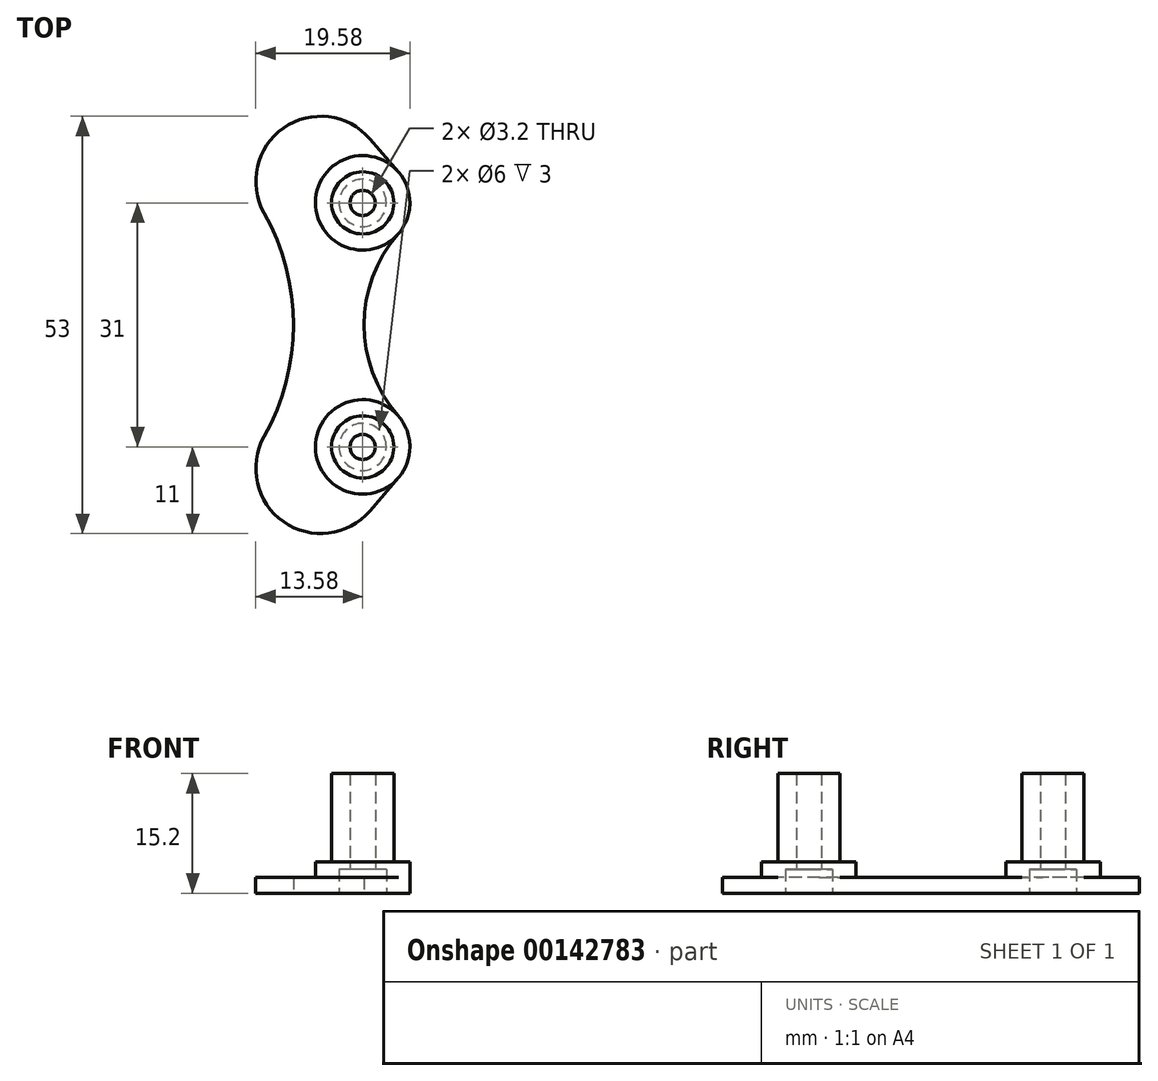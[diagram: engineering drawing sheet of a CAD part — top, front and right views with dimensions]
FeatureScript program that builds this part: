
annotation { "Feature Type Name" : "Feature", "Feature Type Description" : "" }
export const myFeature = defineFeature(function(context is Context, id is Id, definition is map)
    precondition{}
    {
        {
            var Q0;
            Q0=qCreatedBy(makeId("Top.planeOp"),FACE);
            var sketch = newSketch(context, id + "F0", { "sketchPlane" : qUnion([Q0])});
            skCircle(sketch, "E0", {"center": v(0, 15.5) * mm, "radius": 1.6 * mm});
            skCircle(sketch, "E1", {"center": v(0, 15.5) * mm, "radius": 3.95 * mm});
            skCircle(sketch, "E2", {"center": v(0, 15.5) * mm, "radius": 6 * mm});
            skCircle(sketch, "E3", {"center": v(0, -15.5) * mm, "radius": 1.6 * mm});
            skCircle(sketch, "E4", {"center": v(0, -15.5) * mm, "radius": 3.95 * mm});
            skCircle(sketch, "E5", {"center": v(0, -15.5) * mm, "radius": 6 * mm});
            skLineSegment(sketch, "E6", {"start": v(0, 15.5) * mm, "end": v(0, -15.5) * mm, "construction": true});
            skCircle(sketch, "E7", {"center": v(-5.33, 18.25) * mm, "radius": 8.25 * mm});
            skCircle(sketch, "E8", {"center": v(-5.33, -18.25) * mm, "radius": 8.25 * mm});
            skArc(sketch, "E9", {"start": v(-12.52, -14.2) * mm, "mid": v(-8.8, 0) * mm, "end": v(-12.52, 14.2) * mm});
            skArc(sketch, "E10", {"start": v(4.5, 11.54) * mm, "mid": v(0.16, 0) * mm, "end": v(4.5, -11.54) * mm});
            skLineSegment(sketch, "E11", {"start": v(-37.8, 0) * mm, "end": v(17.66, 0) * mm, "construction": true});
            skLineSegment(sketch, "E12", {"start": v(0.92, 23.63) * mm, "end": v(4.55, 19.41) * mm});
            skLineSegment(sketch, "E13", {"start": v(0.92, -23.63) * mm, "end": v(4.55, -19.41) * mm});
            skCircle(sketch, "E14", {"center": v(0, 15.5) * mm, "radius": 3 * mm});
            skCircle(sketch, "E15", {"center": v(0, -15.5) * mm, "radius": 3 * mm});
            skSolve(sketch);
        }
        {
            var Q0;
            {var subQ0=sQuery(id+"F0.wireOp",EDGE,"E9");Q0=makeQuery(id+"F0.imprint","IMPRINT",FACE,{"disambiguationData":[TD([[makeQuery(id+"F0.imprint","IMPRINT",EDGE,{"derivedFrom":subQ0}),-1.0]])]});}
            var Q1;
            {var subQ0=sQuery(id+"F0.wireOp",EDGE,"E8");var subQ1=sQuery(id+"F0.wireOp",EDGE,"E5");var subQ2=makeQuery(id+"F0.imprint","INTERSECT",VERTEX,{"disambiguationData":[OD(0.0)],"derivedFrom":[subQ1,subQ0]});Q1=makeQuery(id+"F0.imprint","IMPRINT",FACE,{"disambiguationData":[TD([[makeQuery(id+"F0.imprint","IMPRINT",EDGE,{"disambiguationData":[TD([[subQ2,-1.0]])],"derivedFrom":subQ1}),-1.0]])]});}
            var Q2;
            {var subQ2=sQuery(id+"F0.wireOp",EDGE,"E8");var subQ5=sQuery(id+"F0.wireOp",EDGE,"E4");var subQ6=makeQuery(id+"F0.imprint","INTERSECT",VERTEX,{"disambiguationData":[OD(0.0)],"derivedFrom":[subQ5,subQ2]});Q2=makeQuery(id+"F0.imprint","IMPRINT",FACE,{"disambiguationData":[TD([[makeQuery(id+"F0.imprint","IMPRINT",EDGE,{"disambiguationData":[TD([[subQ6,1.0]])],"derivedFrom":subQ5}),-1.0]])]});}
            var Q3;
            {var subQ3=sQuery(id+"F0.wireOp",EDGE,"E7");var subQ5=sQuery(id+"F0.wireOp",EDGE,"E1");var subQ8=makeQuery(id+"F0.imprint","INTERSECT",VERTEX,{"disambiguationData":[OD(0.0)],"derivedFrom":[subQ5,subQ3]});Q3=makeQuery(id+"F0.imprint","IMPRINT",FACE,{"disambiguationData":[TD([[makeQuery(id+"F0.imprint","IMPRINT",EDGE,{"disambiguationData":[TD([[subQ8,-1.0]])],"derivedFrom":subQ5}),-1.0]])]});}
            var Q4;
            {var subQ0=sQuery(id+"F0.wireOp",EDGE,"E8");var subQ1=sQuery(id+"F0.wireOp",EDGE,"E4");var subQ2=makeQuery(id+"F0.imprint","INTERSECT",VERTEX,{"disambiguationData":[OD(0.0)],"derivedFrom":[subQ1,subQ0]});Q4=makeQuery(id+"F0.imprint","IMPRINT",FACE,{"disambiguationData":[TD([[makeQuery(id+"F0.imprint","IMPRINT",EDGE,{"disambiguationData":[TD([[subQ2,-1.0]])],"derivedFrom":subQ1}),-1.0]])]});}
            var Q5;
            {var subQ0=sQuery(id+"F0.wireOp",EDGE,"E7");var subQ1=sQuery(id+"F0.wireOp",EDGE,"E2");var subQ2=makeQuery(id+"F0.imprint","INTERSECT",VERTEX,{"disambiguationData":[OD(0.0)],"derivedFrom":[subQ1,subQ0]});Q5=makeQuery(id+"F0.imprint","IMPRINT",FACE,{"disambiguationData":[TD([[makeQuery(id+"F0.imprint","IMPRINT",EDGE,{"disambiguationData":[TD([[subQ2,-1.0]])],"derivedFrom":subQ1}),-1.0]])]});}
            var Q6;
            {var subQ0=sQuery(id+"F0.wireOp",EDGE,"E7");var subQ1=sQuery(id+"F0.wireOp",EDGE,"E1");var subQ2=makeQuery(id+"F0.imprint","INTERSECT",VERTEX,{"disambiguationData":[OD(0.0)],"derivedFrom":[subQ1,subQ0]});Q6=makeQuery(id+"F0.imprint","IMPRINT",FACE,{"disambiguationData":[TD([[makeQuery(id+"F0.imprint","IMPRINT",EDGE,{"disambiguationData":[TD([[subQ2,1.0]])],"derivedFrom":subQ1}),-1.0]])]});}
            var Q7;
            Q7=makeQuery(id+"F0.imprint","IMPRINT",FACE,{"disambiguationData":[TD([[makeQuery(id+"F0.imprint","IMPRINT",EDGE,{"derivedFrom":sQuery(id+"F0.wireOp",EDGE,"E0")}),-1.0]])]});
            var Q8;
            Q8=makeQuery(id+"F0.imprint","IMPRINT",FACE,{"disambiguationData":[TD([[makeQuery(id+"F0.imprint","IMPRINT",EDGE,{"derivedFrom":sQuery(id+"F0.wireOp",EDGE,"E3")}),-1.0]])]});
            var Q9;
            Q9=makeQuery(id+"F0.imprint","IMPRINT",FACE,{"disambiguationData":[TD([[makeQuery(id+"F0.imprint","IMPRINT",EDGE,{"derivedFrom":sQuery(id+"F0.wireOp",EDGE,"E3")}),1.0]])]});
            var Q10;
            Q10=makeQuery(id+"F0.imprint","IMPRINT",FACE,{"disambiguationData":[TD([[makeQuery(id+"F0.imprint","IMPRINT",EDGE,{"derivedFrom":sQuery(id+"F0.wireOp",EDGE,"E0")}),1.0]])]});
            var Q11;
            {var subQ0=sQuery(id+"F0.wireOp",EDGE,"E8");var subQ1=sQuery(id+"F0.wireOp",EDGE,"E4");var subQ2=makeQuery(id+"F0.imprint","INTERSECT",VERTEX,{"disambiguationData":[OD(0.0)],"derivedFrom":[subQ1,subQ0]});Q11=makeQuery(id+"F0.imprint","IMPRINT",FACE,{"disambiguationData":[TD([[makeQuery(id+"F0.imprint","IMPRINT",EDGE,{"disambiguationData":[TD([[subQ2,1.0]])],"derivedFrom":subQ1}),1.0]])]});}
            var Q12;
            {var subQ0=sQuery(id+"F0.wireOp",EDGE,"E7");var subQ1=sQuery(id+"F0.wireOp",EDGE,"E1");var subQ2=makeQuery(id+"F0.imprint","INTERSECT",VERTEX,{"disambiguationData":[OD(0.0)],"derivedFrom":[subQ1,subQ0]});Q12=makeQuery(id+"F0.imprint","IMPRINT",FACE,{"disambiguationData":[TD([[makeQuery(id+"F0.imprint","IMPRINT",EDGE,{"disambiguationData":[TD([[subQ2,-1.0]])],"derivedFrom":subQ1}),1.0]])]});}
            var Q13;
            {var subQ0=sQuery(id+"F0.wireOp",EDGE,"E12");Q13=makeQuery(id+"F0.imprint","IMPRINT",FACE,{"disambiguationData":[TD([[makeQuery(id+"F0.imprint","IMPRINT",EDGE,{"derivedFrom":subQ0}),-1.0]])]});}
            var Q14;
            {var subQ0=sQuery(id+"F0.wireOp",EDGE,"E13");Q14=makeQuery(id+"F0.imprint","IMPRINT",FACE,{"disambiguationData":[TD([[makeQuery(id+"F0.imprint","IMPRINT",EDGE,{"derivedFrom":subQ0}),1.0]])]});}
            var Q15;
            {var subQ0=sQuery(id+"F0.wireOp",EDGE,"E7");var subQ1=sQuery(id+"F0.wireOp",EDGE,"E1");var subQ2=makeQuery(id+"F0.imprint","INTERSECT",VERTEX,{"disambiguationData":[OD(0.0)],"derivedFrom":[subQ1,subQ0]});Q15=makeQuery(id+"F0.imprint","IMPRINT",FACE,{"disambiguationData":[TD([[makeQuery(id+"F0.imprint","IMPRINT",EDGE,{"disambiguationData":[TD([[subQ2,1.0]])],"derivedFrom":subQ1}),1.0]])]});}
            var Q16;
            {var subQ0=sQuery(id+"F0.wireOp",EDGE,"E14");var subQ1=sQuery(id+"F0.wireOp",EDGE,"E7");var subQ2=makeQuery(id+"F0.imprint","INTERSECT",VERTEX,{"disambiguationData":[OD(0.0)],"derivedFrom":[subQ1,subQ0]});Q16=makeQuery(id+"F0.imprint","IMPRINT",FACE,{"disambiguationData":[TD([[makeQuery(id+"F0.imprint","IMPRINT",EDGE,{"disambiguationData":[TD([[subQ2,-1.0]])],"derivedFrom":subQ1}),-1.0]])]});}
            var Q17;
            {var subQ0=sQuery(id+"F0.wireOp",EDGE,"E8");var subQ1=sQuery(id+"F0.wireOp",EDGE,"E4");var subQ2=makeQuery(id+"F0.imprint","INTERSECT",VERTEX,{"disambiguationData":[OD(0.0)],"derivedFrom":[subQ1,subQ0]});Q17=makeQuery(id+"F0.imprint","IMPRINT",FACE,{"disambiguationData":[TD([[makeQuery(id+"F0.imprint","IMPRINT",EDGE,{"disambiguationData":[TD([[subQ2,-1.0]])],"derivedFrom":subQ1}),1.0]])]});}
            var Q18;
            {var subQ0=sQuery(id+"F0.wireOp",EDGE,"E15");var subQ1=sQuery(id+"F0.wireOp",EDGE,"E8");var subQ2=makeQuery(id+"F0.imprint","INTERSECT",VERTEX,{"disambiguationData":[OD(0.0)],"derivedFrom":[subQ1,subQ0]});Q18=makeQuery(id+"F0.imprint","IMPRINT",FACE,{"disambiguationData":[TD([[makeQuery(id+"F0.imprint","IMPRINT",EDGE,{"disambiguationData":[TD([[subQ2,-1.0]])],"derivedFrom":subQ1}),-1.0]])]});}
            extrude(context, id + "F1", {"entities" : qUnion([Q0, Q1, Q2, Q3, Q4, Q5, Q6, Q7, Q8, Q9, Q10, Q11, Q12, Q13, Q14, Q15, Q16, Q17, Q18]), "depth" : 2 * mm});
        }
        {
            var Q0;
            {var subQ0=sQuery(id+"F0.wireOp",EDGE,"E8");var subQ1=sQuery(id+"F0.wireOp",EDGE,"E4");var subQ2=makeQuery(id+"F0.imprint","INTERSECT",VERTEX,{"disambiguationData":[OD(0.0)],"derivedFrom":[subQ1,subQ0]});Q0=makeQuery(id+"F0.imprint","IMPRINT",FACE,{"disambiguationData":[TD([[makeQuery(id+"F0.imprint","IMPRINT",EDGE,{"disambiguationData":[TD([[subQ2,-1.0]])],"derivedFrom":subQ1}),-1.0]])]});}
            var Q1;
            {var subQ2=sQuery(id+"F0.wireOp",EDGE,"E8");var subQ5=sQuery(id+"F0.wireOp",EDGE,"E4");var subQ6=makeQuery(id+"F0.imprint","INTERSECT",VERTEX,{"disambiguationData":[OD(0.0)],"derivedFrom":[subQ5,subQ2]});Q1=makeQuery(id+"F0.imprint","IMPRINT",FACE,{"disambiguationData":[TD([[makeQuery(id+"F0.imprint","IMPRINT",EDGE,{"disambiguationData":[TD([[subQ6,1.0]])],"derivedFrom":subQ5}),-1.0]])]});}
            var Q2;
            {var subQ3=sQuery(id+"F0.wireOp",EDGE,"E7");var subQ5=sQuery(id+"F0.wireOp",EDGE,"E1");var subQ8=makeQuery(id+"F0.imprint","INTERSECT",VERTEX,{"disambiguationData":[OD(0.0)],"derivedFrom":[subQ5,subQ3]});Q2=makeQuery(id+"F0.imprint","IMPRINT",FACE,{"disambiguationData":[TD([[makeQuery(id+"F0.imprint","IMPRINT",EDGE,{"disambiguationData":[TD([[subQ8,-1.0]])],"derivedFrom":subQ5}),-1.0]])]});}
            var Q3;
            {var subQ0=sQuery(id+"F0.wireOp",EDGE,"E7");var subQ1=sQuery(id+"F0.wireOp",EDGE,"E1");var subQ2=makeQuery(id+"F0.imprint","INTERSECT",VERTEX,{"disambiguationData":[OD(0.0)],"derivedFrom":[subQ1,subQ0]});Q3=makeQuery(id+"F0.imprint","IMPRINT",FACE,{"disambiguationData":[TD([[makeQuery(id+"F0.imprint","IMPRINT",EDGE,{"disambiguationData":[TD([[subQ2,1.0]])],"derivedFrom":subQ1}),-1.0]])]});}
            var Q4;
            Q4=makeQuery(id+"F0.imprint","IMPRINT",FACE,{"disambiguationData":[TD([[makeQuery(id+"F0.imprint","IMPRINT",EDGE,{"derivedFrom":sQuery(id+"F0.wireOp",EDGE,"E0")}),-1.0]])]});
            var Q5;
            Q5=makeQuery(id+"F0.imprint","IMPRINT",FACE,{"disambiguationData":[TD([[makeQuery(id+"F0.imprint","IMPRINT",EDGE,{"derivedFrom":sQuery(id+"F0.wireOp",EDGE,"E3")}),-1.0]])]});
            var Q6;
            Q6=makeQuery(id+"F0.imprint","IMPRINT",FACE,{"disambiguationData":[TD([[makeQuery(id+"F0.imprint","IMPRINT",EDGE,{"derivedFrom":sQuery(id+"F0.wireOp",EDGE,"E3")}),1.0]])]});
            var Q7;
            Q7=makeQuery(id+"F0.imprint","IMPRINT",FACE,{"disambiguationData":[TD([[makeQuery(id+"F0.imprint","IMPRINT",EDGE,{"derivedFrom":sQuery(id+"F0.wireOp",EDGE,"E0")}),1.0]])]});
            var Q8;
            {var subQ0=sQuery(id+"F0.wireOp",EDGE,"E7");var subQ1=sQuery(id+"F0.wireOp",EDGE,"E1");var subQ2=makeQuery(id+"F0.imprint","INTERSECT",VERTEX,{"disambiguationData":[OD(0.0)],"derivedFrom":[subQ1,subQ0]});Q8=makeQuery(id+"F0.imprint","IMPRINT",FACE,{"disambiguationData":[TD([[makeQuery(id+"F0.imprint","IMPRINT",EDGE,{"disambiguationData":[TD([[subQ2,-1.0]])],"derivedFrom":subQ1}),1.0]])]});}
            var Q9;
            {var subQ0=sQuery(id+"F0.wireOp",EDGE,"E8");var subQ1=sQuery(id+"F0.wireOp",EDGE,"E4");var subQ2=makeQuery(id+"F0.imprint","INTERSECT",VERTEX,{"disambiguationData":[OD(0.0)],"derivedFrom":[subQ1,subQ0]});Q9=makeQuery(id+"F0.imprint","IMPRINT",FACE,{"disambiguationData":[TD([[makeQuery(id+"F0.imprint","IMPRINT",EDGE,{"disambiguationData":[TD([[subQ2,1.0]])],"derivedFrom":subQ1}),1.0]])]});}
            var Q10;
            {var subQ0=sQuery(id+"F0.wireOp",EDGE,"E7");var subQ1=sQuery(id+"F0.wireOp",EDGE,"E1");var subQ2=makeQuery(id+"F0.imprint","INTERSECT",VERTEX,{"disambiguationData":[OD(0.0)],"derivedFrom":[subQ1,subQ0]});Q10=makeQuery(id+"F0.imprint","IMPRINT",FACE,{"disambiguationData":[TD([[makeQuery(id+"F0.imprint","IMPRINT",EDGE,{"disambiguationData":[TD([[subQ2,1.0]])],"derivedFrom":subQ1}),1.0]])]});}
            var Q11;
            {var subQ0=sQuery(id+"F0.wireOp",EDGE,"E14");var subQ1=sQuery(id+"F0.wireOp",EDGE,"E7");var subQ2=makeQuery(id+"F0.imprint","INTERSECT",VERTEX,{"disambiguationData":[OD(0.0)],"derivedFrom":[subQ1,subQ0]});Q11=makeQuery(id+"F0.imprint","IMPRINT",FACE,{"disambiguationData":[TD([[makeQuery(id+"F0.imprint","IMPRINT",EDGE,{"disambiguationData":[TD([[subQ2,-1.0]])],"derivedFrom":subQ1}),-1.0]])]});}
            var Q12;
            {var subQ0=sQuery(id+"F0.wireOp",EDGE,"E15");var subQ1=sQuery(id+"F0.wireOp",EDGE,"E8");var subQ2=makeQuery(id+"F0.imprint","INTERSECT",VERTEX,{"disambiguationData":[OD(0.0)],"derivedFrom":[subQ1,subQ0]});Q12=makeQuery(id+"F0.imprint","IMPRINT",FACE,{"disambiguationData":[TD([[makeQuery(id+"F0.imprint","IMPRINT",EDGE,{"disambiguationData":[TD([[subQ2,-1.0]])],"derivedFrom":subQ1}),-1.0]])]});}
            var Q13;
            {var subQ0=sQuery(id+"F0.wireOp",EDGE,"E8");var subQ1=sQuery(id+"F0.wireOp",EDGE,"E4");var subQ2=makeQuery(id+"F0.imprint","INTERSECT",VERTEX,{"disambiguationData":[OD(0.0)],"derivedFrom":[subQ1,subQ0]});Q13=makeQuery(id+"F0.imprint","IMPRINT",FACE,{"disambiguationData":[TD([[makeQuery(id+"F0.imprint","IMPRINT",EDGE,{"disambiguationData":[TD([[subQ2,-1.0]])],"derivedFrom":subQ1}),1.0]])]});}
            extrude(context, id + "F2", {"entities" : qUnion([Q0, Q1, Q2, Q3, Q4, Q5, Q6, Q7, Q8, Q9, Q10, Q11, Q12, Q13]), "operationType" : NewBodyOperationType.ADD, "depth" : 4 * mm});
        }
        {
            var Q0;
            {var subQ0=sQuery(id+"F0.wireOp",EDGE,"E8");var subQ1=sQuery(id+"F0.wireOp",EDGE,"E4");var subQ2=makeQuery(id+"F0.imprint","INTERSECT",VERTEX,{"disambiguationData":[OD(0.0)],"derivedFrom":[subQ1,subQ0]});Q0=makeQuery(id+"F0.imprint","IMPRINT",FACE,{"disambiguationData":[TD([[makeQuery(id+"F0.imprint","IMPRINT",EDGE,{"disambiguationData":[TD([[subQ2,1.0]])],"derivedFrom":subQ1}),1.0]])]});}
            var Q1;
            Q1=makeQuery(id+"F0.imprint","IMPRINT",FACE,{"disambiguationData":[TD([[makeQuery(id+"F0.imprint","IMPRINT",EDGE,{"derivedFrom":sQuery(id+"F0.wireOp",EDGE,"E3")}),-1.0]])]});
            var Q2;
            Q2=makeQuery(id+"F0.imprint","IMPRINT",FACE,{"disambiguationData":[TD([[makeQuery(id+"F0.imprint","IMPRINT",EDGE,{"derivedFrom":sQuery(id+"F0.wireOp",EDGE,"E3")}),1.0]])]});
            var Q3;
            Q3=makeQuery(id+"F0.imprint","IMPRINT",FACE,{"disambiguationData":[TD([[makeQuery(id+"F0.imprint","IMPRINT",EDGE,{"derivedFrom":sQuery(id+"F0.wireOp",EDGE,"E0")}),-1.0]])]});
            var Q4;
            Q4=makeQuery(id+"F0.imprint","IMPRINT",FACE,{"disambiguationData":[TD([[makeQuery(id+"F0.imprint","IMPRINT",EDGE,{"derivedFrom":sQuery(id+"F0.wireOp",EDGE,"E0")}),1.0]])]});
            var Q5;
            {var subQ0=sQuery(id+"F0.wireOp",EDGE,"E7");var subQ1=sQuery(id+"F0.wireOp",EDGE,"E1");var subQ2=makeQuery(id+"F0.imprint","INTERSECT",VERTEX,{"disambiguationData":[OD(0.0)],"derivedFrom":[subQ1,subQ0]});Q5=makeQuery(id+"F0.imprint","IMPRINT",FACE,{"disambiguationData":[TD([[makeQuery(id+"F0.imprint","IMPRINT",EDGE,{"disambiguationData":[TD([[subQ2,1.0]])],"derivedFrom":subQ1}),1.0]])]});}
            var Q6;
            {var subQ0=sQuery(id+"F0.wireOp",EDGE,"E7");var subQ1=sQuery(id+"F0.wireOp",EDGE,"E1");var subQ2=makeQuery(id+"F0.imprint","INTERSECT",VERTEX,{"disambiguationData":[OD(0.0)],"derivedFrom":[subQ1,subQ0]});Q6=makeQuery(id+"F0.imprint","IMPRINT",FACE,{"disambiguationData":[TD([[makeQuery(id+"F0.imprint","IMPRINT",EDGE,{"disambiguationData":[TD([[subQ2,-1.0]])],"derivedFrom":subQ1}),1.0]])]});}
            var Q7;
            {var subQ0=sQuery(id+"F0.wireOp",EDGE,"E14");var subQ1=sQuery(id+"F0.wireOp",EDGE,"E7");var subQ2=makeQuery(id+"F0.imprint","INTERSECT",VERTEX,{"disambiguationData":[OD(0.0)],"derivedFrom":[subQ1,subQ0]});Q7=makeQuery(id+"F0.imprint","IMPRINT",FACE,{"disambiguationData":[TD([[makeQuery(id+"F0.imprint","IMPRINT",EDGE,{"disambiguationData":[TD([[subQ2,-1.0]])],"derivedFrom":subQ1}),-1.0]])]});}
            var Q8;
            {var subQ0=sQuery(id+"F0.wireOp",EDGE,"E8");var subQ1=sQuery(id+"F0.wireOp",EDGE,"E4");var subQ2=makeQuery(id+"F0.imprint","INTERSECT",VERTEX,{"disambiguationData":[OD(0.0)],"derivedFrom":[subQ1,subQ0]});Q8=makeQuery(id+"F0.imprint","IMPRINT",FACE,{"disambiguationData":[TD([[makeQuery(id+"F0.imprint","IMPRINT",EDGE,{"disambiguationData":[TD([[subQ2,-1.0]])],"derivedFrom":subQ1}),1.0]])]});}
            var Q9;
            {var subQ0=sQuery(id+"F0.wireOp",EDGE,"E15");var subQ1=sQuery(id+"F0.wireOp",EDGE,"E8");var subQ2=makeQuery(id+"F0.imprint","INTERSECT",VERTEX,{"disambiguationData":[OD(0.0)],"derivedFrom":[subQ1,subQ0]});Q9=makeQuery(id+"F0.imprint","IMPRINT",FACE,{"disambiguationData":[TD([[makeQuery(id+"F0.imprint","IMPRINT",EDGE,{"disambiguationData":[TD([[subQ2,-1.0]])],"derivedFrom":subQ1}),-1.0]])]});}
            extrude(context, id + "F3", {"entities" : qUnion([Q0, Q1, Q2, Q3, Q4, Q5, Q6, Q7, Q8, Q9]), "operationType" : NewBodyOperationType.ADD, "depth" : 15.2 * mm});
        }
        {
            var Q0;
            Q0=makeQuery(id+"F0.imprint","IMPRINT",FACE,{"disambiguationData":[TD([[makeQuery(id+"F0.imprint","IMPRINT",EDGE,{"derivedFrom":sQuery(id+"F0.wireOp",EDGE,"E3")}),1.0]])]});
            var Q1;
            Q1=makeQuery(id+"F0.imprint","IMPRINT",FACE,{"disambiguationData":[TD([[makeQuery(id+"F0.imprint","IMPRINT",EDGE,{"derivedFrom":sQuery(id+"F0.wireOp",EDGE,"E0")}),1.0]])]});
            var Q2;
            Q2=makeQuery(id+"F3.opExtrude","CAP_FACE",FACE,{"disambiguationData":[OSD([sQuery(id+"F0.wireOp",EDGE,"E1")])],"isStart":false});
            extrude(context, id + "F4", {"entities" : qUnion([Q0, Q1]), "operationType" : NewBodyOperationType.REMOVE, "endBound" : BoundingType.UP_TO_SURFACE, "endBoundEntityFace" : qUnion([Q2]), "depth" : 25 * mm});
        }
        {
            var Q0;
            Q0=makeQuery(id+"F0.imprint","IMPRINT",FACE,{"disambiguationData":[TD([[makeQuery(id+"F0.imprint","IMPRINT",EDGE,{"derivedFrom":sQuery(id+"F0.wireOp",EDGE,"E0")}),-1.0]])]});
            var Q1;
            {var subQ0=sQuery(id+"F0.wireOp",EDGE,"E14");var subQ1=sQuery(id+"F0.wireOp",EDGE,"E7");var subQ2=makeQuery(id+"F0.imprint","INTERSECT",VERTEX,{"disambiguationData":[OD(0.0)],"derivedFrom":[subQ1,subQ0]});Q1=makeQuery(id+"F0.imprint","IMPRINT",FACE,{"disambiguationData":[TD([[makeQuery(id+"F0.imprint","IMPRINT",EDGE,{"disambiguationData":[TD([[subQ2,-1.0]])],"derivedFrom":subQ1}),-1.0]])]});}
            var Q2;
            Q2=makeQuery(id+"F0.imprint","IMPRINT",FACE,{"disambiguationData":[TD([[makeQuery(id+"F0.imprint","IMPRINT",EDGE,{"derivedFrom":sQuery(id+"F0.wireOp",EDGE,"E3")}),-1.0]])]});
            var Q3;
            {var subQ0=sQuery(id+"F0.wireOp",EDGE,"E15");var subQ1=sQuery(id+"F0.wireOp",EDGE,"E8");var subQ2=makeQuery(id+"F0.imprint","INTERSECT",VERTEX,{"disambiguationData":[OD(0.0)],"derivedFrom":[subQ1,subQ0]});Q3=makeQuery(id+"F0.imprint","IMPRINT",FACE,{"disambiguationData":[TD([[makeQuery(id+"F0.imprint","IMPRINT",EDGE,{"disambiguationData":[TD([[subQ2,-1.0]])],"derivedFrom":subQ1}),-1.0]])]});}
            var Q4;
            Q4=makeQuery(id+"F0.imprint","IMPRINT",FACE,{"disambiguationData":[TD([[makeQuery(id+"F0.imprint","IMPRINT",EDGE,{"derivedFrom":sQuery(id+"F0.wireOp",EDGE,"E3")}),1.0]])]});
            var Q5;
            Q5=makeQuery(id+"F0.imprint","IMPRINT",FACE,{"disambiguationData":[TD([[makeQuery(id+"F0.imprint","IMPRINT",EDGE,{"derivedFrom":sQuery(id+"F0.wireOp",EDGE,"E0")}),1.0]])]});
            extrude(context, id + "F5", {"entities" : qUnion([Q0, Q1, Q2, Q3, Q4, Q5]), "operationType" : NewBodyOperationType.REMOVE, "depth" : 3 * mm});
        }
    });
